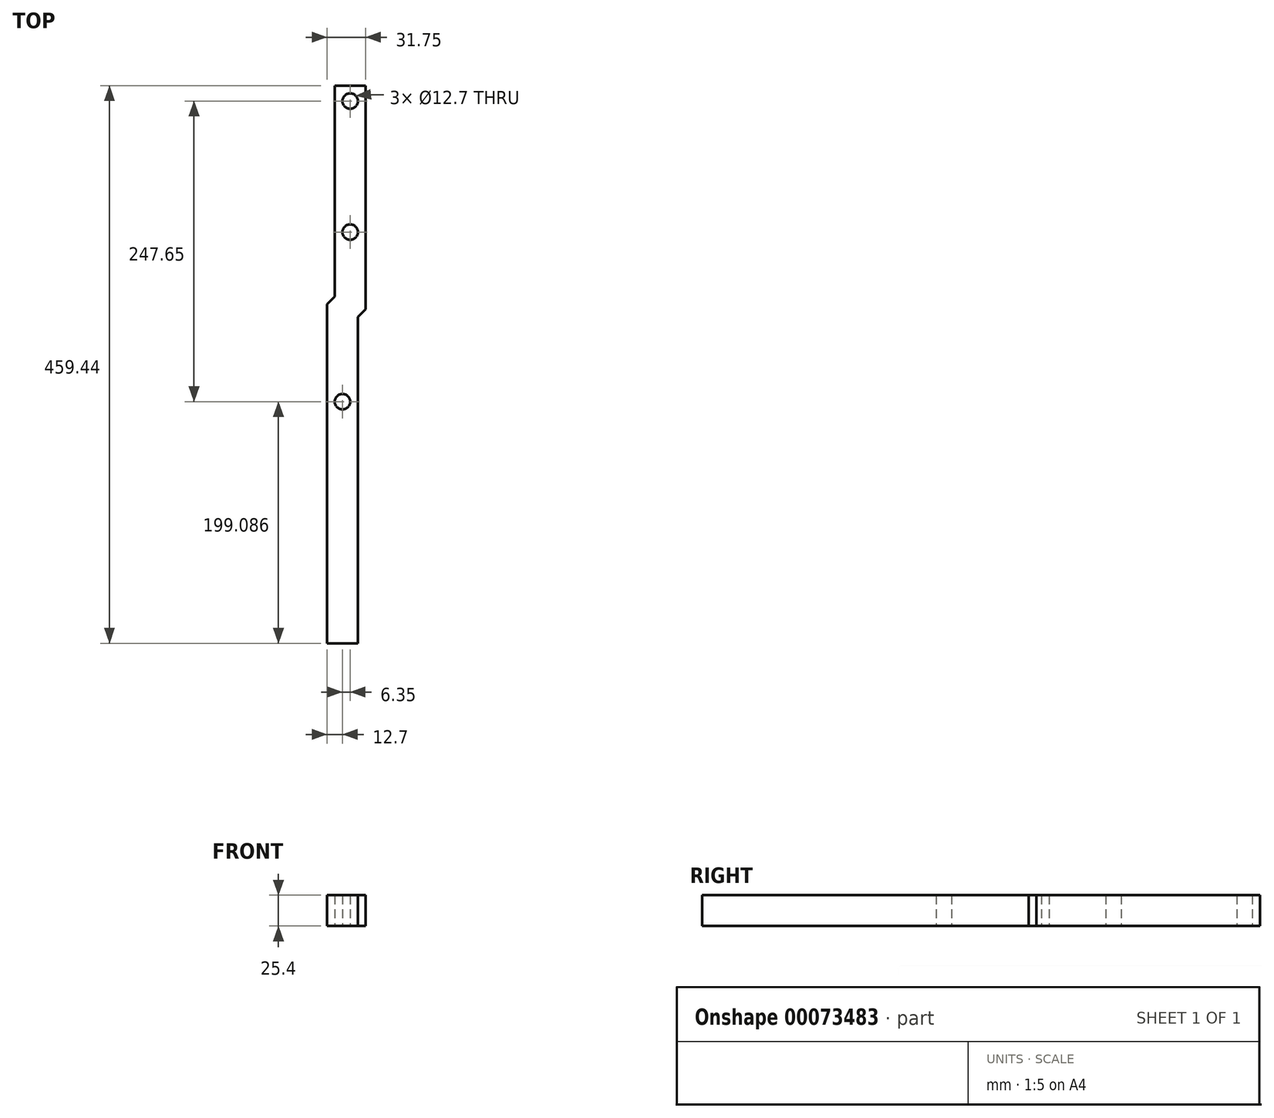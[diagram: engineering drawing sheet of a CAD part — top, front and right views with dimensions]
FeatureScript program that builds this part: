
annotation { "Feature Type Name" : "Feature", "Feature Type Description" : "" }
export const myFeature = defineFeature(function(context is Context, id is Id, definition is map)
    precondition{}
    {
        {
            var Q0;
            Q0=qCreatedBy(makeId("Top.planeOp"),FACE);
            var sketch = newSketch(context, id + "F0", { "sketchPlane" : qUnion([Q0])});
            skLineSegment(sketch, "E0", {"start": v(-20.48, -279.4) * mm, "end": v(-20.48, 0) * mm});
            skLineSegment(sketch, "E1", {"start": v(-20.48, 0) * mm, "end": v(-14.13, 6.35) * mm});
            skLineSegment(sketch, "E2", {"start": v(-14.13, 6.35) * mm, "end": v(-14.13, 180.04) * mm});
            skLineSegment(sketch, "E3", {"start": v(-14.13, 180.04) * mm, "end": v(11.27, 180.04) * mm});
            skLineSegment(sketch, "E4", {"start": v(-20.48, -279.4) * mm, "end": v(4.92, -279.4) * mm});
            skLineSegment(sketch, "E5", {"start": v(11.27, -4.17) * mm, "end": v(4.92, -10.52) * mm});
            skLineSegment(sketch, "E6", {"start": v(11.27, 180.04) * mm, "end": v(11.27, -4.17) * mm});
            skLineSegment(sketch, "E7", {"start": v(4.92, -10.52) * mm, "end": v(4.92, -279.4) * mm});
            skCircle(sketch, "E8", {"center": v(-1.43, 167.34) * mm, "radius": 6.35 * mm});
            skPoint(sketch, "E8.centerSnap0", {"position": v(-1.43, 180.04) * mm});
            skCircle(sketch, "E9", {"center": v(-1.43, 59.39) * mm, "radius": 6.35 * mm});
            skCircle(sketch, "E10", {"center": v(-7.78, -80.31) * mm, "radius": 6.35 * mm});
            skPoint(sketch, "E10.centerSnap0", {"position": v(-7.78, -279.4) * mm});
            skSolve(sketch);
        }
        {
            var Q0;
            Q0=makeQuery(id+"F0.imprint","IMPRINT",FACE,{"disambiguationData":[TD([[makeQuery(id+"F0.imprint","IMPRINT",EDGE,{"derivedFrom":sQuery(id+"F0.wireOp",EDGE,"E0")}),-1.0]])]});
            extrude(context, id + "F1", {"entities" : qUnion([Q0]), "depth" : 25.4 * mm});
        }
    });
